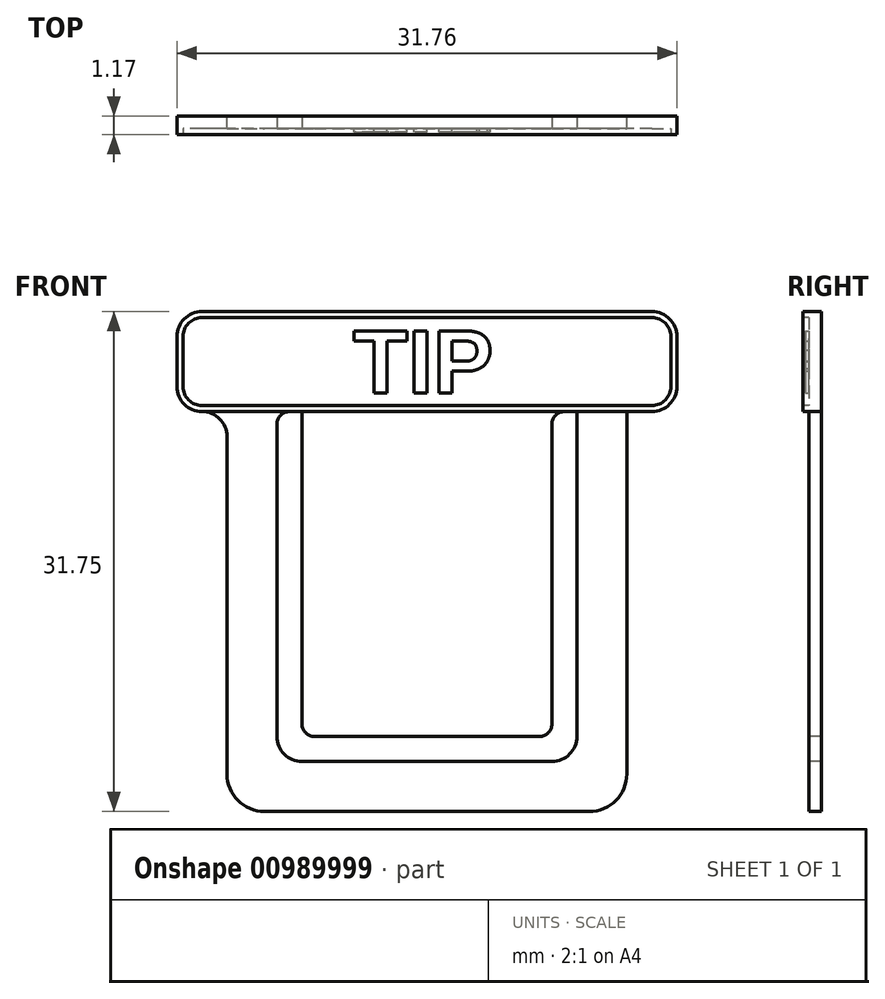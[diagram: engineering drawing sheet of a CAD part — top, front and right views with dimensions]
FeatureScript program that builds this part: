
annotation { "Feature Type Name" : "Feature", "Feature Type Description" : "" }
export const myFeature = defineFeature(function(context is Context, id is Id, definition is map)
    precondition{}
    {
        {
            var Q0;
            Q0=qCreatedBy(makeId("Front.planeOp"),FACE);
            var sketch = newSketch(context, id + "F0", { "sketchPlane" : qUnion([Q0])});
            skLineSegment(sketch, "E0.bottom", {"start": v(12.7, 12.7) * mm, "end": v(-12.7, 12.7) * mm});
            skLineSegment(sketch, "E0.top", {"start": v(12.7, -12.7) * mm, "end": v(-12.7, -12.7) * mm});
            skLineSegment(sketch, "E0.left", {"start": v(12.7, 12.7) * mm, "end": v(12.7, -12.7) * mm});
            skLineSegment(sketch, "E0.right", {"start": v(-12.7, 12.7) * mm, "end": v(-12.7, -12.7) * mm});
            skPoint(sketch, "E0.middle", {"position": v(0, 0) * mm});
            skSolve(sketch);
        }
        {
            var Q0;
            Q0=makeQuery(id+"F0.imprint","IMPRINT",FACE,{"disambiguationData":[TD([[makeQuery(id+"F0.imprint","IMPRINT",EDGE,{"derivedFrom":sQuery(id+"F0.wireOp",EDGE,"E0.bottom")}),1.0]])]});
            extrude(context, id + "F1", {"entities" : qUnion([Q0]), "depth" : 0.8 * mm, "offsetDistance" : 25.4 * mm});
        }
        {
            var Q0;
            Q0=makeQuery(id+"F1.opExtrude","SWEPT_EDGE",EDGE,{"disambiguationData":[OSD([sQuery(id+"F0.wireOp",EDGE,"E0.top"),sQuery(id+"F0.wireOp",EDGE,"E0.left")])]});
            var Q1;
            Q1=makeQuery(id+"F1.opExtrude","SWEPT_EDGE",EDGE,{"disambiguationData":[OSD([sQuery(id+"F0.wireOp",EDGE,"E0.top"),sQuery(id+"F0.wireOp",EDGE,"E0.right")])]});
            fillet(context, id + "F2", {"entities" : qUnion([Q0, Q1]), "radius" : 2.38 * mm, "tangentPropagation" : true, "allowEdgeOverflow" : false});
        }
        {
            var Q0;
            Q0=makeQuery(id+"F1.opExtrude","CAP_FACE",FACE,{"disambiguationData":[OSD([sQuery(id+"F0.wireOp",EDGE,"E0.bottom"),sQuery(id+"F0.wireOp",EDGE,"E0.top"),sQuery(id+"F0.wireOp",EDGE,"E0.left"),sQuery(id+"F0.wireOp",EDGE,"E0.right")])],"isStart":false});
            var sketch = newSketch(context, id + "F3", { "sketchPlane" : qUnion([Q0])});
            skLineSegment(sketch, "E1.bottom", {"start": v(9.52, 12.7) * mm, "end": v(-9.53, 12.7) * mm});
            skLineSegment(sketch, "E1.top", {"start": v(9.53, -9.53) * mm, "end": v(-9.52, -9.53) * mm});
            skLineSegment(sketch, "E1.left", {"start": v(9.52, 12.7) * mm, "end": v(9.53, -9.53) * mm});
            skLineSegment(sketch, "E1.right", {"start": v(-9.53, 12.7) * mm, "end": v(-9.52, -9.53) * mm});
            skPoint(sketch, "E1.middle", {"position": v(0, 0) * mm});
            skSolve(sketch);
        }
        {
            var Q0;
            Q0=makeQuery(id+"F3.imprint","IMPRINT",FACE,{"disambiguationData":[TD([[makeQuery(id+"F3.imprint","IMPRINT",EDGE,{"derivedFrom":sQuery(id+"F3.wireOp",EDGE,"E1.bottom")}),1.0]])]});
            extrude(context, id + "F4", {"entities" : qUnion([Q0]), "operationType" : NewBodyOperationType.REMOVE, "oppositeDirection" : true, "depth" : 4.93 * mm, "offsetDistance" : 25.4 * mm});
        }
        {
            var Q0;
            Q0=makeQuery(id+"F1.opExtrude","CAP_FACE",FACE,{"disambiguationData":[OSD([sQuery(id+"F0.wireOp",EDGE,"E0.bottom"),sQuery(id+"F0.wireOp",EDGE,"E0.top"),sQuery(id+"F0.wireOp",EDGE,"E0.left"),sQuery(id+"F0.wireOp",EDGE,"E0.right")])],"isStart":false});
            var sketch = newSketch(context, id + "F5", { "sketchPlane" : qUnion([Q0])});
            skLineSegment(sketch, "E2.bottom", {"start": v(-15.88, 12.7) * mm, "end": v(15.88, 12.7) * mm});
            skLineSegment(sketch, "E2.top", {"start": v(-15.88, 19.05) * mm, "end": v(15.88, 19.05) * mm});
            skLineSegment(sketch, "E2.left", {"start": v(-15.88, 12.7) * mm, "end": v(-15.88, 19.05) * mm});
            skLineSegment(sketch, "E2.right", {"start": v(15.87, 12.7) * mm, "end": v(15.87, 19.05) * mm});
            skSolve(sketch);
        }
        {
            var Q0;
            Q0=makeQuery(id+"F5.imprint","IMPRINT",FACE,{"disambiguationData":[TD([[makeQuery(id+"F5.imprint","IMPRINT",EDGE,{"derivedFrom":sQuery(id+"F5.wireOp",EDGE,"E2.top")}),-1.0]])]});
            extrude(context, id + "F6", {"entities" : qUnion([Q0]), "operationType" : NewBodyOperationType.ADD, "oppositeDirection" : true, "depth" : 0.8 * mm, "offsetDistance" : 25.4 * mm});
        }
        {
            var Q0;
            Q0=makeQuery(id+"F6.opExtrude","SWEPT_EDGE",EDGE,{"disambiguationData":[OSD([sQuery(id+"F5.wireOp",EDGE,"E2.top"),sQuery(id+"F5.wireOp",EDGE,"E2.left")])]});
            var Q1;
            Q1=makeQuery(id+"F6.opExtrude","SWEPT_EDGE",EDGE,{"disambiguationData":[OSD([sQuery(id+"F5.wireOp",EDGE,"E2.top"),sQuery(id+"F5.wireOp",EDGE,"E2.right")])]});
            var Q2;
            Q2=makeQuery(id+"F6.opExtrude","SWEPT_EDGE",EDGE,{"disambiguationData":[OSD([sQuery(id+"F5.wireOp",EDGE,"E2.bottom"),sQuery(id+"F5.wireOp",EDGE,"E2.right")])]});
            var Q3;
            Q3=makeQuery(id+"F1.opExtrude","SWEPT_EDGE",EDGE,{"disambiguationData":[OSD([sQuery(id+"F0.wireOp",EDGE,"E0.bottom"),sQuery(id+"F0.wireOp",EDGE,"E0.left")])]});
            var Q4;
            Q4=makeQuery(id+"F6.opExtrude","SWEPT_EDGE",EDGE,{"disambiguationData":[OSD([sQuery(id+"F5.wireOp",EDGE,"E2.bottom"),sQuery(id+"F5.wireOp",EDGE,"E2.left")])]});
            var Q5;
            Q5=makeQuery(id+"F1.opExtrude","SWEPT_EDGE",EDGE,{"disambiguationData":[OSD([sQuery(id+"F0.wireOp",EDGE,"E0.bottom"),sQuery(id+"F0.wireOp",EDGE,"E0.right")])]});
            fillet(context, id + "F7", {"entities" : qUnion([Q0, Q1, Q2, Q3, Q4, Q5]), "radius" : 1.59 * mm, "tangentPropagation" : true, "allowEdgeOverflow" : false});
        }
        {
            var Q0;
            Q0=makeQuery(id+"F4.boolean.opBoolean","COPY",EDGE,{"derivedFrom":makeQuery(id+"F4.opExtrude","SWEPT_EDGE",EDGE,{"disambiguationData":[OSD([sQuery(id+"F3.wireOp",EDGE,"E1.top"),sQuery(id+"F3.wireOp",EDGE,"E1.right")])]})});
            var Q1;
            Q1=makeQuery(id+"F4.boolean.opBoolean","COPY",EDGE,{"derivedFrom":makeQuery(id+"F4.opExtrude","SWEPT_EDGE",EDGE,{"disambiguationData":[OSD([sQuery(id+"F3.wireOp",EDGE,"E1.top"),sQuery(id+"F3.wireOp",EDGE,"E1.left")])]})});
            fillet(context, id + "F8", {"entities" : qUnion([Q0, Q1]), "radius" : 1.59 * mm, "tangentPropagation" : true, "allowEdgeOverflow" : false});
        }
        {
            var Q0;
            Q0=makeQuery(id+"F6.boolean.opBoolean","MERGE",FACE,{"derivedFrom":[makeQuery(id+"F1.opExtrude","CAP_FACE",FACE,{"disambiguationData":[OSD([sQuery(id+"F0.wireOp",EDGE,"E0.bottom"),sQuery(id+"F0.wireOp",EDGE,"E0.top"),sQuery(id+"F0.wireOp",EDGE,"E0.left"),sQuery(id+"F0.wireOp",EDGE,"E0.right")])],"isStart":false}),makeQuery(id+"F6.opExtrude","CAP_FACE",FACE,{"disambiguationData":[OSD([sQuery(id+"F5.wireOp",EDGE,"E2.bottom"),sQuery(id+"F5.wireOp",EDGE,"E2.top"),sQuery(id+"F5.wireOp",EDGE,"E2.left"),sQuery(id+"F5.wireOp",EDGE,"E2.right")])],"isStart":true})]});
            var sketch = newSketch(context, id + "F9", { "sketchPlane" : qUnion([Q0])});
            skLineSegment(sketch, "E3.bottom", {"start": v(-7.94, 12.7) * mm, "end": v(7.94, 12.7) * mm});
            skLineSegment(sketch, "E3.top", {"start": v(-7.94, -7.94) * mm, "end": v(7.94, -7.94) * mm});
            skLineSegment(sketch, "E3.left", {"start": v(-7.94, 12.7) * mm, "end": v(-7.94, -7.94) * mm});
            skLineSegment(sketch, "E3.right", {"start": v(7.94, 12.7) * mm, "end": v(7.94, -7.94) * mm});
            skSolve(sketch);
        }
        {
            var Q0;
            Q0=makeQuery(id+"F9.imprint","IMPRINT",FACE,{"disambiguationData":[TD([[makeQuery(id+"F9.imprint","IMPRINT",EDGE,{"derivedFrom":sQuery(id+"F9.wireOp",EDGE,"E3.bottom")}),1.0]])]});
            extrude(context, id + "F10", {"entities" : qUnion([Q0]), "operationType" : NewBodyOperationType.ADD, "oppositeDirection" : true, "depth" : 0.8 * mm, "offsetDistance" : 25.4 * mm});
        }
        {
            var Q0;
            Q0=makeQuery(id+"F10.opExtrude","SWEPT_EDGE",EDGE,{"disambiguationData":[OSD([sQuery(id+"F5.wireOp",EDGE,"E2.bottom"),sQuery(id+"F9.wireOp",EDGE,"E3.bottom"),sQuery(id+"F9.wireOp",EDGE,"E3.left")])]});
            var Q1;
            Q1=makeQuery(id+"F4.boolean.opBoolean","COPY",EDGE,{"derivedFrom":makeQuery(id+"F4.opExtrude","SWEPT_EDGE",EDGE,{"disambiguationData":[OSD([sQuery(id+"F0.wireOp",EDGE,"E0.bottom"),sQuery(id+"F3.wireOp",EDGE,"E1.bottom"),sQuery(id+"F3.wireOp",EDGE,"E1.right")])]})});
            var Q2;
            Q2=makeQuery(id+"F10.opExtrude","SWEPT_EDGE",EDGE,{"disambiguationData":[OSD([sQuery(id+"F5.wireOp",EDGE,"E2.bottom"),sQuery(id+"F9.wireOp",EDGE,"E3.bottom"),sQuery(id+"F9.wireOp",EDGE,"E3.right")])]});
            var Q3;
            Q3=makeQuery(id+"F4.boolean.opBoolean","COPY",EDGE,{"derivedFrom":makeQuery(id+"F4.opExtrude","SWEPT_EDGE",EDGE,{"disambiguationData":[OSD([sQuery(id+"F0.wireOp",EDGE,"E0.bottom"),sQuery(id+"F3.wireOp",EDGE,"E1.bottom"),sQuery(id+"F3.wireOp",EDGE,"E1.left")])]})});
            fillet(context, id + "F11", {"entities" : qUnion([Q0, Q1, Q2, Q3]), "radius" : 0.8 * mm, "tangentPropagation" : true, "allowEdgeOverflow" : false});
        }
        {
            var Q0;
            Q0=makeQuery(id+"F10.opExtrude","SWEPT_EDGE",EDGE,{"disambiguationData":[OSD([sQuery(id+"F9.wireOp",EDGE,"E3.top"),sQuery(id+"F9.wireOp",EDGE,"E3.left")])]});
            var Q1;
            Q1=makeQuery(id+"F10.opExtrude","SWEPT_EDGE",EDGE,{"disambiguationData":[OSD([sQuery(id+"F9.wireOp",EDGE,"E3.top"),sQuery(id+"F9.wireOp",EDGE,"E3.right")])]});
            fillet(context, id + "F12", {"entities" : qUnion([Q0, Q1]), "radius" : 0.8 * mm, "tangentPropagation" : true, "allowEdgeOverflow" : false});
        }
        {
            var Q0;
            Q0=makeQuery(id+"F10.boolean.opBoolean","MERGE",FACE,{"derivedFrom":[makeQuery(id+"F6.boolean.opBoolean","MERGE",FACE,{"derivedFrom":[makeQuery(id+"F1.opExtrude","CAP_FACE",FACE,{"disambiguationData":[OSD([sQuery(id+"F0.wireOp",EDGE,"E0.bottom"),sQuery(id+"F0.wireOp",EDGE,"E0.top"),sQuery(id+"F0.wireOp",EDGE,"E0.left"),sQuery(id+"F0.wireOp",EDGE,"E0.right")])],"isStart":false}),makeQuery(id+"F6.opExtrude","CAP_FACE",FACE,{"disambiguationData":[OSD([sQuery(id+"F5.wireOp",EDGE,"E2.bottom"),sQuery(id+"F5.wireOp",EDGE,"E2.top"),sQuery(id+"F5.wireOp",EDGE,"E2.left"),sQuery(id+"F5.wireOp",EDGE,"E2.right")])],"isStart":true})]}),makeQuery(id+"F10.opExtrude","CAP_FACE",FACE,{"disambiguationData":[OSD([sQuery(id+"F9.wireOp",EDGE,"E3.bottom"),sQuery(id+"F9.wireOp",EDGE,"E3.top"),sQuery(id+"F9.wireOp",EDGE,"E3.left"),sQuery(id+"F9.wireOp",EDGE,"E3.right")])],"isStart":true})]});
            var sketch = newSketch(context, id + "F13", { "sketchPlane" : qUnion([Q0])});
            skArc(sketch, "E4.0", {"start": v(-14.29, 19.05) * mm, "mid": v(-15.41, 18.59) * mm, "end": v(-15.88, 17.46) * mm});
            skLineSegment(sketch, "E5.0", {"start": v(-15.88, 14.29) * mm, "end": v(-15.88, 17.46) * mm});
            skArc(sketch, "E6.0", {"start": v(-15.88, 14.29) * mm, "mid": v(-15.41, 13.16) * mm, "end": v(-14.29, 12.7) * mm});
            skLineSegment(sketch, "E7.0", {"start": v(-14.29, 19.05) * mm, "end": v(14.29, 19.05) * mm});
            skArc(sketch, "E8.0", {"start": v(15.87, 17.46) * mm, "mid": v(15.41, 18.59) * mm, "end": v(14.29, 19.05) * mm});
            skLineSegment(sketch, "E9.0", {"start": v(15.87, 14.29) * mm, "end": v(15.87, 17.46) * mm});
            skArc(sketch, "E10.0", {"start": v(14.29, 12.7) * mm, "mid": v(15.41, 13.16) * mm, "end": v(15.87, 14.29) * mm});
            skLineSegment(sketch, "E11", {"start": v(-14.29, 12.7) * mm, "end": v(14.29, 12.7) * mm});
            skSolve(sketch);
        }
        {
            var Q0;
            Q0=makeQuery(id+"F13.imprint","IMPRINT",FACE,{"disambiguationData":[TD([[makeQuery(id+"F13.imprint","IMPRINT",EDGE,{"derivedFrom":sQuery(id+"F13.wireOp",EDGE,"E4.0")}),1.0]])]});
            extrude(context, id + "F14", {"entities" : qUnion([Q0]), "operationType" : NewBodyOperationType.ADD, "depth" : 0.38 * mm, "offsetDistance" : 25.4 * mm});
        }
        {
            var Q0;
            Q0=makeQuery(id+"F14.opExtrude","CAP_FACE",FACE,{"disambiguationData":[OSD([sQuery(id+"F13.wireOp",EDGE,"E4.0"),sQuery(id+"F13.wireOp",EDGE,"E5.0"),sQuery(id+"F13.wireOp",EDGE,"E6.0"),sQuery(id+"F13.wireOp",EDGE,"E7.0"),sQuery(id+"F13.wireOp",EDGE,"E8.0"),sQuery(id+"F13.wireOp",EDGE,"E9.0"),sQuery(id+"F13.wireOp",EDGE,"E10.0"),sQuery(id+"F13.wireOp",EDGE,"E11")])],"isStart":false});
            var sketch = newSketch(context, id + "F15", { "sketchPlane" : qUnion([Q0])});
            skArc(sketch, "E12.0", {"start": v(-14.29, 19.05) * mm, "mid": v(-15.41, 18.59) * mm, "end": v(-15.88, 17.46) * mm});
            skLineSegment(sketch, "E13.0", {"start": v(-14.29, 19.05) * mm, "end": v(14.29, 19.05) * mm});
            skLineSegment(sketch, "E14.0", {"start": v(-15.88, 14.29) * mm, "end": v(-15.88, 17.46) * mm});
            skArc(sketch, "E15.0", {"start": v(-15.88, 14.29) * mm, "mid": v(-15.41, 13.16) * mm, "end": v(-14.29, 12.7) * mm});
            skLineSegment(sketch, "E16.0", {"start": v(-14.29, 12.7) * mm, "end": v(14.29, 12.7) * mm});
            skArc(sketch, "E17.0", {"start": v(14.29, 12.7) * mm, "mid": v(15.41, 13.16) * mm, "end": v(15.87, 14.29) * mm});
            skArc(sketch, "E18.0", {"start": v(15.87, 17.46) * mm, "mid": v(15.41, 18.59) * mm, "end": v(14.29, 19.05) * mm});
            skArc(sketch, "E19", {"start": v(-14.29, 18.67) * mm, "mid": v(-15.14, 18.32) * mm, "end": v(-15.5, 17.46) * mm});
            skArc(sketch, "E20", {"start": v(-15.5, 14.29) * mm, "mid": v(-15.14, 13.43) * mm, "end": v(-14.29, 13.08) * mm});
            skArc(sketch, "E21", {"start": v(15.5, 17.46) * mm, "mid": v(15.14, 18.32) * mm, "end": v(14.29, 18.67) * mm});
            skArc(sketch, "E22", {"start": v(14.29, 13.08) * mm, "mid": v(15.14, 13.43) * mm, "end": v(15.5, 14.29) * mm});
            skLineSegment(sketch, "E23", {"start": v(-14.29, 19.05) * mm, "end": v(-14.29, 12.7) * mm, "construction": true});
            skLineSegment(sketch, "E24", {"start": v(-15.88, 17.46) * mm, "end": v(15.87, 17.46) * mm, "construction": true});
            skLineSegment(sketch, "E25", {"start": v(14.29, 19.05) * mm, "end": v(14.29, 12.7) * mm, "construction": true});
            skLineSegment(sketch, "E26", {"start": v(15.87, 14.29) * mm, "end": v(-15.88, 14.29) * mm, "construction": true});
            skLineSegment(sketch, "E27", {"start": v(14.29, 18.67) * mm, "end": v(-14.29, 18.67) * mm});
            skLineSegment(sketch, "E28", {"start": v(-15.5, 17.46) * mm, "end": v(-15.5, 14.29) * mm});
            skLineSegment(sketch, "E29", {"start": v(-14.29, 13.08) * mm, "end": v(14.29, 13.08) * mm});
            skLineSegment(sketch, "E30", {"start": v(15.5, 17.46) * mm, "end": v(15.5, 14.29) * mm});
            skSolve(sketch);
        }
        {
            var Q0;
            Q0=makeQuery(id+"F15.imprint","IMPRINT",FACE,{"disambiguationData":[TD([[makeQuery(id+"F15.imprint","IMPRINT",EDGE,{"derivedFrom":sQuery(id+"F15.wireOp",EDGE,"E19")}),1.0]])]});
            var Q1;
            {var subQ0=sQuery(id+"F9.wireOp",EDGE,"E3.right");var subQ1=sQuery(id+"F9.wireOp",EDGE,"E3.top");var subQ3=sQuery(id+"F0.wireOp",EDGE,"E0.bottom");var subQ4=sQuery(id+"F9.wireOp",EDGE,"E3.left");var subQ5=makeQuery(id+"F6.opExtrude","CAP_FACE",FACE,{"disambiguationData":[OSD([sQuery(id+"F5.wireOp",EDGE,"E2.bottom"),sQuery(id+"F5.wireOp",EDGE,"E2.top"),sQuery(id+"F5.wireOp",EDGE,"E2.left"),sQuery(id+"F5.wireOp",EDGE,"E2.right")])],"isStart":true});var subQ6=makeQuery(id+"F1.opExtrude","CAP_FACE",FACE,{"disambiguationData":[OSD([subQ3,sQuery(id+"F0.wireOp",EDGE,"E0.top"),sQuery(id+"F0.wireOp",EDGE,"E0.left"),sQuery(id+"F0.wireOp",EDGE,"E0.right")])],"isStart":false});var subQ7=makeQuery(id+"F10.opExtrude","CAP_FACE",FACE,{"disambiguationData":[OSD([sQuery(id+"F9.wireOp",EDGE,"E3.bottom"),subQ1,subQ4,subQ0])],"isStart":true});Q1=makeQuery(id+"F14.boolean.opBoolean","SPLIT",FACE,{"disambiguationData":[TD([makeQuery(id+"F10.opExtrude","SWEPT_FACE",FACE,{"disambiguationData":[OSD([subQ1])]})])],"derivedFrom":makeQuery(id+"F10.boolean.opBoolean","MERGE",FACE,{"derivedFrom":[makeQuery(id+"F6.boolean.opBoolean","MERGE",FACE,{"derivedFrom":[subQ6,subQ5]}),subQ7]})});}
            extrude(context, id + "F16", {"entities" : qUnion([Q0]), "operationType" : NewBodyOperationType.REMOVE, "endBound" : BoundingType.UP_TO_SURFACE, "oppositeDirection" : true, "depth" : 25.4 * mm, "endBoundEntityFace" : qUnion([Q1]), "offsetDistance" : 25.4 * mm});
        }
        {
            var Q0;
            Q0=qCreatedBy(makeId("Front.planeOp"),FACE);
            var sketch = newSketch(context, id + "F17", { "sketchPlane" : qUnion([Q0])});
            skText(sketch, "E31", { "text": "TIP", "fontName": "Arimo-Bold.ttf"});
            const initialGuessF17  = {"E31": [-0.0047, 0.01388, 1, 0, 0.00412]};
            skSetInitialGuess(sketch, initialGuessF17);
            skSolve(sketch);
        }
        {
            var Q0;
            Q0=qSketchRegion(id+"F17",true);
            extrude(context, id + "F18", {"entities" : qUnion([Q0]), "operationType" : NewBodyOperationType.ADD, "depth" : 1.02 * mm, "offsetDistance" : 25.4 * mm});
        }
    });
